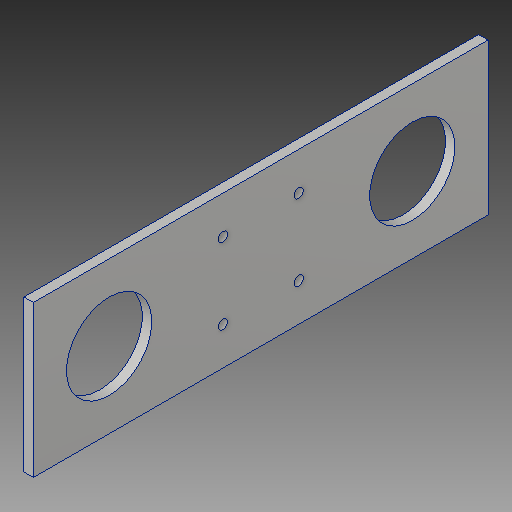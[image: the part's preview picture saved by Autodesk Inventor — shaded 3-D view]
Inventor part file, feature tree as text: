
AUTODESK INVENTOR PART (.ipt)
format: ipt  version: 2017 (Build 210142000, 142)  size: 114,176 bytes
history: native  units: in
note: dims shown in document units (in); Inventor stores cm internally (conversion verified against a paired STEP export)
features: extrude x1, sketch x1
ambient origin geometry x8: Origin, YZ Plane, XZ Plane, XY Plane, X Axis, Y Axis, Z Axis, Center Point
bodies: Body1 (feature_tree)
feature tree (2):
  extrude  "Extrusion2"  Depth=6.0in
  sketch  "Sketch1"  dims[d11=2.0in d12=6.0in d13=1.0in d14=1.125in d22=0.5in d23=0.5in d24=0.125in d25=0.125in d26=0.0in]
